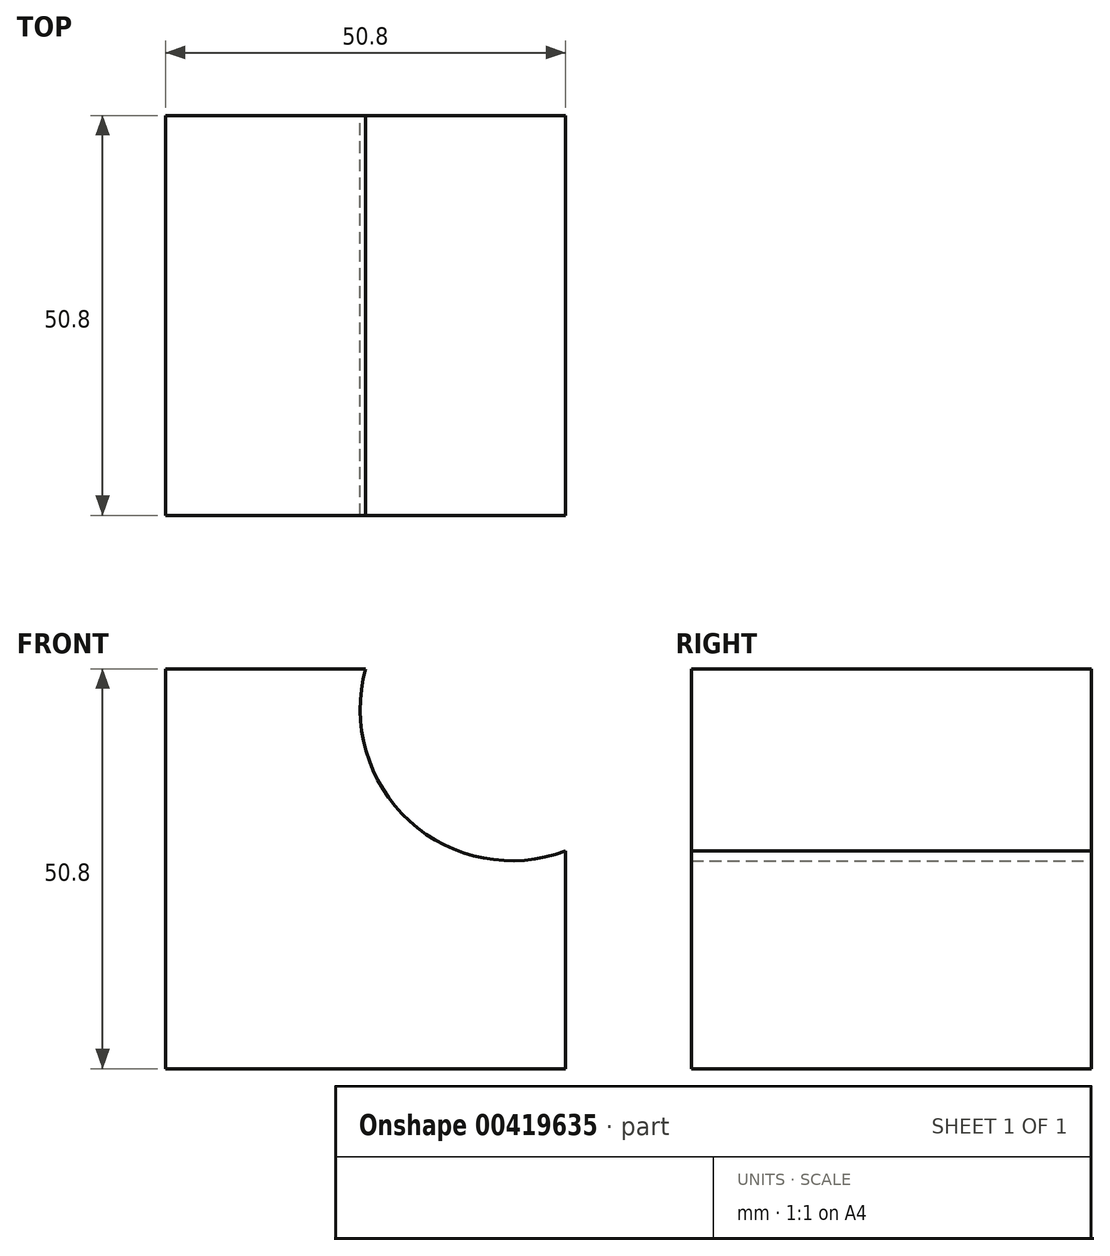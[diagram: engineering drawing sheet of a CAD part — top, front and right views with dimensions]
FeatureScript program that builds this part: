
annotation { "Feature Type Name" : "Feature", "Feature Type Description" : "" }
export const myFeature = defineFeature(function(context is Context, id is Id, definition is map)
    precondition{}
    {
        {
            var Q0;
            Q0=qCreatedBy(makeId("Front.planeOp"),FACE);
            var sketch = newSketch(context, id + "F0", { "sketchPlane" : qUnion([Q0])});
            skLineSegment(sketch, "E0", {"start": v(0, 0) * mm, "end": v(0, 50.8) * mm});
            skLineSegment(sketch, "E1", {"start": v(0, 0) * mm, "end": v(50.8, 0) * mm});
            skLineSegment(sketch, "E2", {"start": v(0, 50.8) * mm, "end": v(25.4, 50.8) * mm});
            skPoint(sketch, "E2.endSnap0", {"position": v(25.4, 0) * mm});
            skLineSegment(sketch, "E3", {"start": v(50.8, 0) * mm, "end": v(50.8, 27.66) * mm});
            skArc(sketch, "E4", {"start": v(25.4, 50.8) * mm, "mid": v(31, 31.44) * mm, "end": v(50.8, 27.66) * mm});
            skSolve(sketch);
        }
        {
            var Q0;
            Q0 = qSketchRegion(id + "F0", true);
            extrude(context, id + "F1", {"entities" : qUnion([Q0]), "depth" : 50.8 * mm});
        }
    });
